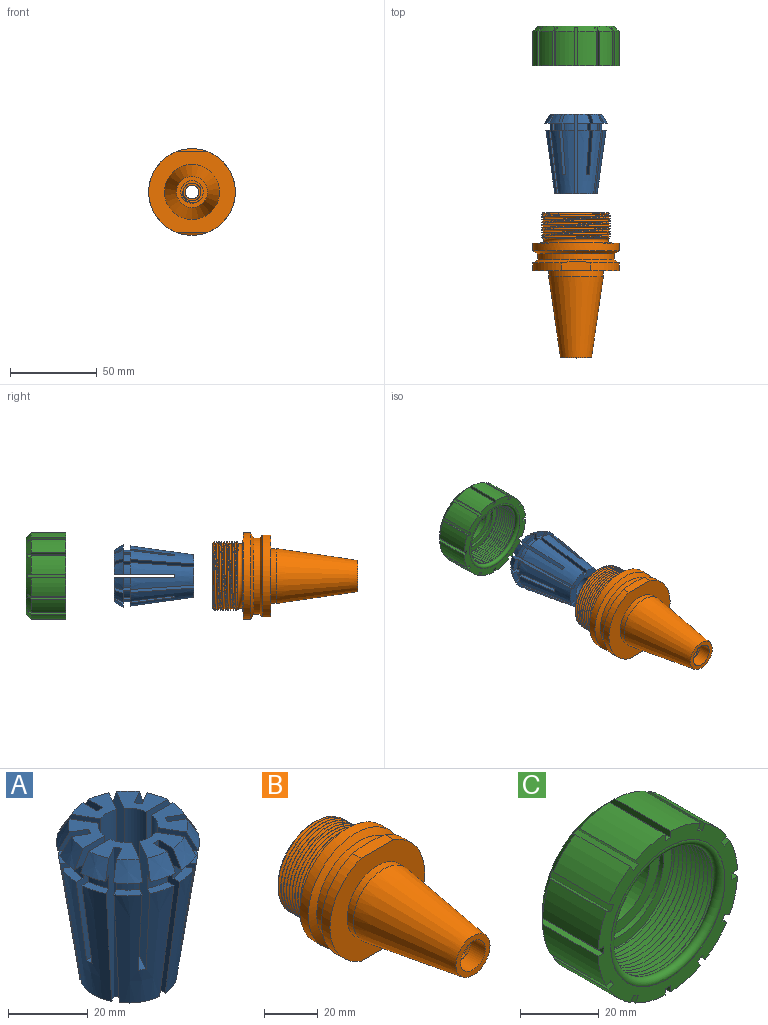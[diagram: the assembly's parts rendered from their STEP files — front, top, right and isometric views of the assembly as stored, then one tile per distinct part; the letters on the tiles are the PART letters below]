
ASSEMBLY  parts=3 mates=2
PART A: 98 faces, bbox 36x36x46.1 mm
  f0: plane 11.46x10.38mm, normal (0,0,1), area 63.4mm2, adj f10,f11,f36,f58,f85,f86,f87,f97
  f1: plane 13.23x8.03mm, normal (0,0,1), area 63.4mm2, adj f8,f9,f41,f62,f82,f83,f84,f97
  f2: plane 11.46x10.38mm, normal (0,0,1), area 63.4mm2, adj f6,f7,f66,f72,f74,f75,f76,f97
  f3: plane 11.46x10.38mm, normal (0,0,1), area 63.4mm2, adj f5,f16,f21,f46,f94,f95,f96,f97
  f4: plane 13.23x8.03mm, normal (0,0,1), area 63.4mm2, adj f14,f15,f26,f50,f91,f92,f93,f97
  f5: plane 35.03x10.57mm, normal (0,1,0), area 287.4mm2, adj f3,f43,f44,f45,f46,f67,f73,f97
  f6: plane 35.03x10.57mm, normal (0,-1,0), area 287.4mm2, adj f2,f63,f64,f65,f66,f67,f73,f97
  f7: plane 35.03x9.15mm, normal (0.87,0.5,0), area 287.4mm2, adj f2,f42,f69,f70,f71,f72,f77,f97
  f8: plane 35.03x9.15mm, normal (-0.87,-0.5,0), area 287.4mm2, adj f1,f38,f39,f40,f41,f42,f77,f97
  f9: plane 35.03x9.15mm, normal (0.87,-0.5,0), area 287.4mm2, adj f1,f37,f59,f60,f61,f62,f78,f97
  f10: plane 35.03x9.15mm, normal (-0.87,0.5,0), area 287.4mm2, adj f0,f33,f34,f35,f36,f37,f78,f97
  f11: plane 35.03x10.57mm, normal (0,-1,0), area 287.4mm2, adj f0,f32,f55,f56,f57,f58,f79,f97
  f12: plane 35.03x10.57mm, normal (0,1,0), area 287.4mm2, adj f17,f28,f29,f30,f31,f32,f79,f97
  f13: plane 35.03x9.15mm, normal (-0.87,-0.5,0), area 287.4mm2, adj f17,f27,f51,f52,f53,f54,f80,f97
  f14: plane 35.03x9.15mm, normal (0.87,0.5,0), area 287.4mm2, adj f4,f23,f24,f25,f26,f27,f80,f97
  f15: plane 35.03x9.15mm, normal (-0.87,0.5,0), area 287.4mm2, adj f4,f22,f47,f48,f49,f50,f81,f97
  f16: plane 35.03x9.15mm, normal (0.87,-0.5,0), area 287.4mm2, adj f3,f18,f19,f20,f21,f22,f81,f97
  f17: plane 11.46x10.38mm, normal (0,0,1), area 63.4mm2, adj f12,f13,f31,f54,f88,f89,f90,f97
  f18: plane 6.22x6.22mm, normal (0,0,1), area 15.7mm2, adj f16,f20,f22,f94
  f19: plane 6.72x6.72mm, normal (0,0,-1), area 19.9mm2, adj f16,f20,f21,f94
  f20: cylinder r=15mm len=4.11mm, axis (0,0,1), area 24mm2, adj f16,f18,f19,f94
  f21: cone r=15mm half-angle=30deg, axis (0,0,-1), area 39.8mm2, adj f3,f16,f19,f94
  f22: cone r=18mm half-angle=8deg, axis (0,0,1), area 448mm2, adj f15,f16,f18,f47,f68,f81,f93,f94
  f23: plane 6.83x3.93mm, normal (0,0,1), area 15.7mm2, adj f14,f25,f27,f91
  f24: plane 7.12x4.51mm, normal (0,0,-1), area 19.9mm2, adj f14,f25,f26,f91
  f25: cylinder r=15mm len=5.62mm, axis (0,0,1), area 24mm2, adj f14,f23,f24,f91
  f26: cone r=15mm half-angle=30deg, axis (0,0,-1), area 39.8mm2, adj f4,f14,f24,f91
  f27: cone r=18mm half-angle=8deg, axis (0,0,1), area 448mm2, adj f13,f14,f23,f51,f68,f80,f90,f91
  f28: plane 6.83x3.93mm, normal (0,0,1), area 15.7mm2, adj f12,f30,f32,f88
  f29: plane 7.12x4.51mm, normal (0,0,-1), area 19.9mm2, adj f12,f30,f31,f88
  f30: cylinder r=15mm len=5.62mm, axis (0,0,1), area 24mm2, adj f12,f28,f29,f88
  f31: cone r=15mm half-angle=30deg, axis (0,0,-1), area 39.8mm2, adj f12,f17,f29,f88
  f32: cone r=18mm half-angle=8deg, axis (0,0,1), area 448mm2, adj f11,f12,f28,f55,f68,f79,f87,f88
  f33: plane 6.22x6.22mm, normal (0,0,1), area 15.7mm2, adj f10,f35,f37,f85
  f34: plane 6.72x6.72mm, normal (0,0,-1), area 19.9mm2, adj f10,f35,f36,f85
  f35: cylinder r=15mm len=4.11mm, axis (0,0,1), area 24mm2, adj f10,f33,f34,f85
  f36: cone r=15mm half-angle=30deg, axis (0,0,-1), area 39.8mm2, adj f0,f10,f34,f85
  f37: cone r=18mm half-angle=8deg, axis (0,0,1), area 448mm2, adj f9,f10,f33,f59,f68,f78,f84,f85
  f38: plane 6.83x3.93mm, normal (0,0,1), area 15.7mm2, adj f8,f40,f42,f82
  f39: plane 7.12x4.51mm, normal (0,0,-1), area 19.9mm2, adj f8,f40,f41,f82
  f40: cylinder r=15mm len=5.62mm, axis (0,0,1), area 24mm2, adj f8,f38,f39,f82
  f41: cone r=15mm half-angle=30deg, axis (0,0,-1), area 39.8mm2, adj f1,f8,f39,f82
  f42: cone r=18mm half-angle=8deg, axis (0,0,1), area 448mm2, adj f7,f8,f38,f68,f69,f76,f77,f82
  f43: plane 6.83x3.93mm, normal (0,0,1), area 15.7mm2, adj f5,f45,f67,f96
  f44: plane 7.12x4.51mm, normal (0,0,-1), area 19.9mm2, adj f5,f45,f46,f96
  f45: cylinder r=15mm len=5.62mm, axis (0,0,1), area 24mm2, adj f5,f43,f44,f96
  f46: cone r=15mm half-angle=30deg, axis (0,0,-1), area 39.8mm2, adj f3,f5,f44,f96
  f47: plane 6.83x3.93mm, normal (0,0,1), area 15.7mm2, adj f15,f22,f49,f93
  f48: plane 7.12x4.51mm, normal (0,0,-1), area 19.9mm2, adj f15,f49,f50,f93
  f49: cylinder r=15mm len=5.62mm, axis (0,0,1), area 24mm2, adj f15,f47,f48,f93
  f50: cone r=15mm half-angle=30deg, axis (0,0,-1), area 39.8mm2, adj f4,f15,f48,f93
  f51: plane 6.22x6.22mm, normal (0,0,1), area 15.7mm2, adj f13,f27,f53,f90
  f52: plane 6.72x6.72mm, normal (0,0,-1), area 19.9mm2, adj f13,f53,f54,f90
  f53: cylinder r=15mm len=4.11mm, axis (0,0,1), area 24mm2, adj f13,f51,f52,f90
  f54: cone r=15mm half-angle=30deg, axis (0,0,-1), area 39.8mm2, adj f13,f17,f52,f90
  f55: plane 6.83x3.93mm, normal (0,0,1), area 15.7mm2, adj f11,f32,f57,f87
  f56: plane 7.12x4.51mm, normal (0,0,-1), area 19.9mm2, adj f11,f57,f58,f87
  f57: cylinder r=15mm len=5.62mm, axis (0,0,1), area 24mm2, adj f11,f55,f56,f87
  f58: cone r=15mm half-angle=30deg, axis (0,0,-1), area 39.8mm2, adj f0,f11,f56,f87
  f59: plane 6.83x3.93mm, normal (0,0,1), area 15.7mm2, adj f9,f37,f61,f84
  f60: plane 7.12x4.51mm, normal (0,0,-1), area 19.9mm2, adj f9,f61,f62,f84
  f61: cylinder r=15mm len=5.62mm, axis (0,0,1), area 24mm2, adj f9,f59,f60,f84
  f62: cone r=15mm half-angle=30deg, axis (0,0,-1), area 39.8mm2, adj f1,f9,f60,f84
  f63: plane 6.83x3.93mm, normal (0,0,1), area 15.7mm2, adj f6,f65,f67,f75
  f64: plane 7.12x4.51mm, normal (0,0,-1), area 19.9mm2, adj f6,f65,f66,f75
  f65: cylinder r=15mm len=5.62mm, axis (0,0,1), area 24mm2, adj f6,f63,f64,f75
  f66: cone r=15mm half-angle=30deg, axis (0,0,-1), area 39.8mm2, adj f2,f6,f64,f75
  f67: cone r=18mm half-angle=8deg, axis (0,0,1), area 448mm2, adj f5,f6,f43,f63,f68,f73,f75,f96
  f68: plane 24.53x24.45mm, normal (0,0,-1), area 268.9mm2, adj f22,f27,f32,f37,f42,f67,f74,f75
  f69: plane 6.22x6.22mm, normal (0,0,1), area 15.7mm2, adj f7,f42,f71,f76
  f70: plane 6.72x6.72mm, normal (0,0,-1), area 19.9mm2, adj f7,f71,f72,f76
  f71: cylinder r=15mm len=4.11mm, axis (0,0,1), area 24mm2, adj f7,f69,f70,f76
  f72: cone r=15mm half-angle=30deg, axis (0,0,-1), area 39.8mm2, adj f2,f7,f70,f76
  f73: plane 6.38x2mm, normal (0,0,1), area 12.6mm2, adj f5,f6,f67,f97
  f74: plane 46x1.73mm, normal (-0.87,0.5,0), area 92mm2, adj f2,f68,f75,f76
  f75: plane 46.06x6.97mm, normal (0.5,0.87,0), area 230.5mm2, adj f2,f63,f64,f65,f66,f67,f68,f74
  f76: plane 46.06x6.97mm, normal (-0.5,-0.87,0), area 230.5mm2, adj f2,f42,f68,f69,f70,f71,f72,f74
  f77: plane 6.49x4.9mm, normal (0,0,1), area 12.6mm2, adj f7,f8,f42,f97
  f78: plane 6.49x4.9mm, normal (0,0,1), area 12.6mm2, adj f9,f10,f37,f97
  f79: plane 6.38x2mm, normal (0,0,1), area 12.6mm2, adj f11,f12,f32,f97
  f80: plane 6.49x4.9mm, normal (0,0,1), area 12.6mm2, adj f13,f14,f27,f97
  f81: plane 6.49x4.9mm, normal (0,0,1), area 12.6mm2, adj f15,f16,f22,f97
  f82: plane 46.06x8.03mm, normal (1,0,0), area 230.5mm2, adj f1,f38,f39,f40,f41,f42,f68,f83
  f83: plane 46x2mm, normal (0,1,0), area 92mm2, adj f1,f68,f82,f84
  f84: plane 46.06x8.03mm, normal (-1,0,0), area 230.5mm2, adj f1,f37,f59,f60,f61,f62,f68,f83
  f85: plane 46.06x6.97mm, normal (0.5,-0.87,0), area 230.5mm2, adj f0,f33,f34,f35,f36,f37,f68,f86
  f86: plane 46x1.73mm, normal (0.87,0.5,0), area 92mm2, adj f0,f68,f85,f87
  f87: plane 46.06x6.97mm, normal (-0.5,0.87,0), area 230.5mm2, adj f0,f32,f55,f56,f57,f58,f68,f86
  f88: plane 46.06x6.97mm, normal (-0.5,-0.87,0), area 230.5mm2, adj f17,f28,f29,f30,f31,f32,f68,f89
  f89: plane 46x1.73mm, normal (0.87,-0.5,0), area 92mm2, adj f17,f68,f88,f90
  f90: plane 46.06x6.97mm, normal (0.5,0.87,0), area 230.5mm2, adj f17,f27,f51,f52,f53,f54,f68,f89
  f91: plane 46.06x8.03mm, normal (-1,0,0), area 230.5mm2, adj f4,f23,f24,f25,f26,f27,f68,f92
  f92: plane 46x2mm, normal (0,-1,0), area 92mm2, adj f4,f68,f91,f93
  f93: plane 46.06x8.03mm, normal (1,0,0), area 230.5mm2, adj f4,f22,f47,f48,f49,f50,f68,f92
  f94: plane 46.06x6.97mm, normal (-0.5,0.87,0), area 230.5mm2, adj f3,f18,f19,f20,f21,f22,f68,f95
  f95: plane 46x1.73mm, normal (-0.87,-0.5,0), area 92mm2, adj f3,f68,f94,f96
  f96: plane 46.06x6.97mm, normal (0.5,-0.87,0), area 230.5mm2, adj f3,f43,f44,f45,f46,f67,f68,f95
  f97: cylinder r=7.5mm len=46mm, axis (0,0,1), area 1746.4mm2, adj f0,f1,f2,f3,f4,f5,f6,f7
PART B: 33 faces, bbox 50.9x85.7x50.9 mm
  f0: cylinder r=4mm len=23.36mm, axis (0,-1,0), area 587mm2, adj f3,f27
  f1: cylinder r=20mm len=40mm, axis (0,-1,0), area 141.4mm2, adj f22,f23,f24,f25
  f2: plane 38x38mm, normal (0,1,0), area 328.8mm2, adj f9,f22,f23,f24
  f3: cone r=11.91mm half-angle=66deg, axis (0,1,0), area 432.9mm2, adj f0,f8
  f4: cone r=32.15mm half-angle=60deg, axis (0,-1,0), area 452.9mm2, adj f6,f7,f13,f17,f18
  f5: plane 50x47mm, normal (0,-1,0), area 1137.4mm2, adj f6,f7,f16,f17,f18
  f6: cylinder r=25mm len=47mm, axis (0,-1,0), area 272.3mm2, adj f4,f5,f17,f18
  f7: cylinder r=25mm len=47mm, axis (0,-1,0), area 272.3mm2, adj f4,f5,f17,f18
  f8: cylinder r=11.91mm len=23.82mm, axis (0,-1,0), area 367.1mm2, adj f3,f9
  f9: cone r=16mm half-angle=8deg, axis (0,1,0), area 2576.3mm2, adj f2,f8
  f10: plane 50x50mm, normal (0,1,0), area 645.7mm2, adj f11,f21
  f11: cylinder r=25mm len=50mm, axis (0,-1,0), area 699.7mm2, adj f10,f12
  f12: cone r=32.15mm half-angle=60deg, axis (0,1,0), area 487.5mm2, adj f11,f13
  f13: cylinder r=22.15mm len=44.3mm, axis (0,-1,0), area 514.9mm2, adj f4,f12
  f14: plane 17.97x17.97mm, normal (0,-1,0), area 120.9mm2, adj f15,f19
  f15: cone r=8.99mm half-angle=8.3deg, axis (0,1,0), area 3731.7mm2, adj f14,f16
  f16: cylinder r=15.88mm len=31.75mm, axis (0,-1,0), area 319.2mm2, adj f5,f15
  f17: plane 17.96x6.21mm, normal (0,0,-1), area 85.8mm2, adj f4,f5,f6,f7
  f18: plane 17.07x5.33mm, normal (0,0,1), area 85.8mm2, adj f4,f5,f6,f7
  f19: cylinder r=6.5mm len=13mm, axis (0,-1,0), area 306.3mm2, adj f14,f20
  f20: plane 13.87x13.87mm, normal (0,-1,0), area 38.3mm2, adj f19,f26,f30,f32
  f21: cylinder r=20.48mm len=40.96mm, axis (0,-1,0), area 10.2mm2, adj f10,f25
  f22: cone r=20mm half-angle=45deg, axis (0,-1,0), area 85.9mm2, adj f1,f2,f23,f24
  f23: bspline ~46.19x40mm, area 1531.8mm2, adj f1,f2,f22,f24,f25
  f24: bspline ~46.19x40mm, area 1541.4mm2, adj f1,f2,f22,f23,f25
  f25: torus R=20mm, axis (0,1,0), area 559.4mm2, adj f1,f21,f23,f24
  f26: cylinder r=5.19mm len=15.5mm, axis (0,-1,0), area 56.2mm2, adj f20,f27,f29,f30,f31,f32
  f27: plane 10.38x10.38mm, normal (0,-1,0), area 34.3mm2, adj f0,f26,f28
  f28: cylinder r=5.19mm len=9.85mm, axis (0,-1,0), area 5.2mm2, adj f27,f29,f31
  f29: plane 1.5x1.3mm, normal (0,0,1), area 1mm2, adj f26,f28,f31,f32
  f30: plane 1.02x0.81mm, normal (-0.78,0,-0.62), area 0.5mm2, adj f20,f26,f31
  f31: bspline ~16.5x14.98mm, area 488.9mm2, adj f26,f28,f29,f30,f32
  f32: bspline ~16.5x14.98mm, area 475.6mm2, adj f20,f26,f29,f31
PART C: 61 faces, bbox 50.2x23.2x50.2 mm
  f0: cylinder r=25mm len=20mm, axis (0,-1,0), area 221.8mm2, adj f3,f44,f56,f58
  f1: plane 21.98x1.72mm, normal (0.5,0,0.87), area 41.6mm2, adj f2,f4,f44,f56
  f2: plane 22.06x1.8mm, normal (0.87,0,-0.5), area 44mm2, adj f1,f3,f44,f56
  f3: plane 21.98x1.72mm, normal (-0.5,0,-0.87), area 41.6mm2, adj f0,f2,f44,f56
  f4: cylinder r=25mm len=20mm, axis (0,-1,0), area 221.8mm2, adj f1,f7,f44,f56
  f5: plane 21.98x1.72mm, normal (0.87,0,0.5), area 41.6mm2, adj f6,f8,f44,f56
  f6: plane 22.06x1.8mm, normal (0.5,0,-0.87), area 44mm2, adj f5,f7,f44,f56
  f7: plane 21.98x1.72mm, normal (-0.87,0,-0.5), area 41.6mm2, adj f4,f6,f44,f56
  f8: cylinder r=25mm len=20mm, axis (0,-1,0), area 221.8mm2, adj f5,f11,f44,f56
  f9: plane 21.98x1.98mm, normal (1,0,0), area 41.6mm2, adj f10,f12,f44,f56
  f10: plane 22.06x2.06mm, normal (0,0,-1), area 44mm2, adj f9,f11,f44,f56
  f11: plane 21.98x1.98mm, normal (-1,0,0), area 41.6mm2, adj f8,f10,f44,f56
  f12: cylinder r=25mm len=20mm, axis (0,-1,0), area 221.8mm2, adj f9,f15,f44,f56
  f13: plane 21.98x1.72mm, normal (0.87,0,-0.5), area 41.6mm2, adj f14,f16,f44,f56
  f14: plane 22.06x1.8mm, normal (-0.5,0,-0.87), area 44mm2, adj f13,f15,f44,f56
  f15: plane 21.98x1.72mm, normal (-0.87,0,0.5), area 41.6mm2, adj f12,f14,f44,f56
  f16: cylinder r=25mm len=20mm, axis (0,-1,0), area 221.8mm2, adj f13,f19,f44,f56
  f17: plane 21.98x1.72mm, normal (0.5,0,-0.87), area 41.6mm2, adj f18,f20,f44,f56
  f18: plane 22.06x1.8mm, normal (-0.87,0,-0.5), area 44mm2, adj f17,f19,f44,f56
  f19: plane 21.98x1.72mm, normal (-0.5,0,0.87), area 41.6mm2, adj f16,f18,f44,f56
  f20: cylinder r=25mm len=20mm, axis (0,-1,0), area 221.8mm2, adj f17,f23,f44,f56
  f21: plane 21.98x1.98mm, normal (0,0,-1), area 41.6mm2, adj f22,f24,f44,f56
  f22: plane 22.06x2.07mm, normal (-1,0,0), area 44mm2, adj f21,f23,f44,f56
  f23: plane 21.98x1.98mm, normal (0,0,1), area 41.6mm2, adj f20,f22,f44,f56
  f24: cylinder r=25mm len=20mm, axis (0,-1,0), area 221.8mm2, adj f21,f27,f44,f56
  f25: plane 21.98x1.72mm, normal (-0.5,0,-0.87), area 41.6mm2, adj f26,f28,f44,f56
  f26: plane 22.06x1.8mm, normal (-0.87,0,0.5), area 44mm2, adj f25,f27,f44,f56
  f27: plane 21.98x1.72mm, normal (0.5,0,0.87), area 41.6mm2, adj f24,f26,f44,f56
  f28: cylinder r=25mm len=20mm, axis (0,-1,0), area 221.8mm2, adj f25,f31,f44,f56
  f29: plane 21.98x1.72mm, normal (-0.87,0,-0.5), area 41.6mm2, adj f30,f32,f44,f56
  f30: plane 22.06x1.8mm, normal (-0.5,0,0.87), area 44mm2, adj f29,f31,f44,f56
  f31: plane 21.98x1.72mm, normal (0.87,0,0.5), area 41.6mm2, adj f28,f30,f44,f56
  f32: cylinder r=25mm len=20mm, axis (0,-1,0), area 221.8mm2, adj f29,f35,f44,f56
  f33: plane 21.98x1.98mm, normal (-1,0,0), area 41.6mm2, adj f34,f36,f44,f56
  f34: plane 22.06x2.07mm, normal (0,0,1), area 44mm2, adj f33,f35,f44,f56
  f35: plane 21.98x1.98mm, normal (1,0,0), area 41.6mm2, adj f32,f34,f44,f56
  f36: cylinder r=25mm len=20mm, axis (0,-1,0), area 221.8mm2, adj f33,f39,f44,f56
  f37: plane 21.98x1.72mm, normal (-0.87,0,0.5), area 41.6mm2, adj f38,f40,f44,f56
  f38: plane 22.06x1.8mm, normal (0.5,0,0.87), area 44mm2, adj f37,f39,f44,f56
  f39: plane 21.98x1.72mm, normal (0.87,0,-0.5), area 41.6mm2, adj f36,f38,f44,f56
  f40: cylinder r=25mm len=20mm, axis (0,-1,0), area 221.8mm2, adj f37,f43,f44,f56
  f41: plane 21.98x1.72mm, normal (-0.5,0,0.87), area 41.6mm2, adj f42,f44,f45,f56
  f42: plane 22.06x1.8mm, normal (0.87,0,0.5), area 44mm2, adj f41,f43,f44,f56
  f43: plane 21.98x1.72mm, normal (0.5,0,-0.87), area 41.6mm2, adj f40,f42,f44,f56
  f44: plane 49.96x49.96mm, normal (0,-1,0), area 597.9mm2, adj f0,f1,f2,f3,f4,f5,f6,f7
  f45: cylinder r=25mm len=20mm, axis (0,-1,0), area 221.8mm2, adj f41,f44,f56,f60
  f46: plane 44x44mm, normal (0,1,0), area 1029.7mm2, adj f56,f57
  f47: torus R=20mm, axis (0,1,0), area 559.4mm2, adj f48,f50,f52,f53
  f48: cylinder r=20mm len=40mm, axis (0,-1,0), area 141.4mm2, adj f47,f51,f52,f53
  f49: plane 38.16x38.16mm, normal (0,-1,0), area 328.8mm2, adj f51,f52,f53,f55
  f50: cylinder r=20.48mm len=40.96mm, axis (0,-1,0), area 10.2mm2, adj f44,f47
  f51: cone r=20mm half-angle=45deg, axis (0,-1,0), area 85.9mm2, adj f48,f49,f52,f53
  f52: bspline ~46.19x40mm, area 1531.8mm2, adj f47,f48,f49,f51,f53
  f53: bspline ~46.19x40mm, area 1541.4mm2, adj f47,f48,f49,f51,f52
  f54: plane 32x32mm, normal (0,-1,0), area 313.4mm2, adj f55,f57
  f55: cylinder r=16mm len=32mm, axis (0,-1,0), area 150.8mm2, adj f49,f54
  f56: cone r=22mm half-angle=45deg, axis (0,-1,0), area 559.2mm2, adj f0,f1,f2,f3,f4,f5,f6,f7
  f57: cylinder r=12.5mm len=25mm, axis (0,1,0), area 314.2mm2, adj f46,f54
  f58: plane 21.98x1.98mm, normal (0,0,1), area 41.6mm2, adj f0,f44,f56,f59
  f59: plane 22.06x2.07mm, normal (1,0,0), area 44mm2, adj f44,f56,f58,f60
  f60: plane 21.98x1.98mm, normal (0,0,-1), area 41.6mm2, adj f44,f45,f56,f59
PLACE A rot(axis=(-1,0,0),90deg) t=(-17.79,70.9,91.71)mm
PLACE B t=(-17.79,-23.97,91.71)mm
PLACE C rot(axis=(0,1,0),0deg) t=(-17.79,78.38,91.71)mm
MATE cylindrical B.f0 <-> C.f57  axis (0,-1,0) through (-17.79,34.46,91.71)mm
MATE cylindrical A.f20 <-> B.f0  axis (0,1,0) through (-17.79,116.9,91.71)mm
